# Revit family: Winkelkonsole mit 2 Streben 300x300x 5
name_source: partatom
category: HLS-Bauteile
revit_build: Autodesk Revit 2017 (Build: 20190507_1515(x64)
units: mm (PartAtom-declared; Revit-internal decimal feet)

## family parameters
Basisbauteil = Fläche
Beim Laden mit Abzugskörper schneiden = Nein
Bemaßung runder Anschluss = Durchmesser verwenden
Gemeinsam genutzt = Ja
Raumberechnungspunkt = Nein
Teiletyp = Normal

## types (1)
- Konsole mit 2 Streben 300x300x 5
    Abmessung = 300 x 300 x 5 mm
    Artikelnummer = 0814091
    EAN = 4250928419811
    Fabrikat = MEFA
    Firma = MEFA Befestigungs- und Montagesysteme GmbH
    Gewicht = 1.68 kg
    Gewicht pro Bauteil = 1.68 kg
    Höhe = 300 mm
    Kurztext1 = Winkelkonsole mit 2 Streben
    Kurztext2 = 300 x 300 x 5 mm
    L = 300 mm
    Last bei Länge = 250 mm
    Länge = 300 mm
    Material = Stahl
    Materialname = S235
    Mengeneinheit = St
    Oberflaeche = galvanisch verzinkt
    Stärke = 5 mm  [stored 0.0164042 ft]
    Vorgabe-Ansicht = 1219 mm
    max. zul. Last = 1.12 kip
    max. zul. Last F1 = 0.00 kip
    max. zul. Last F2 = 0.00 kip
    vpe = 10 St

note: [stored X ft] marks values corroborated as IEEE doubles in the binary element streams (Revit-internal decimal feet)
